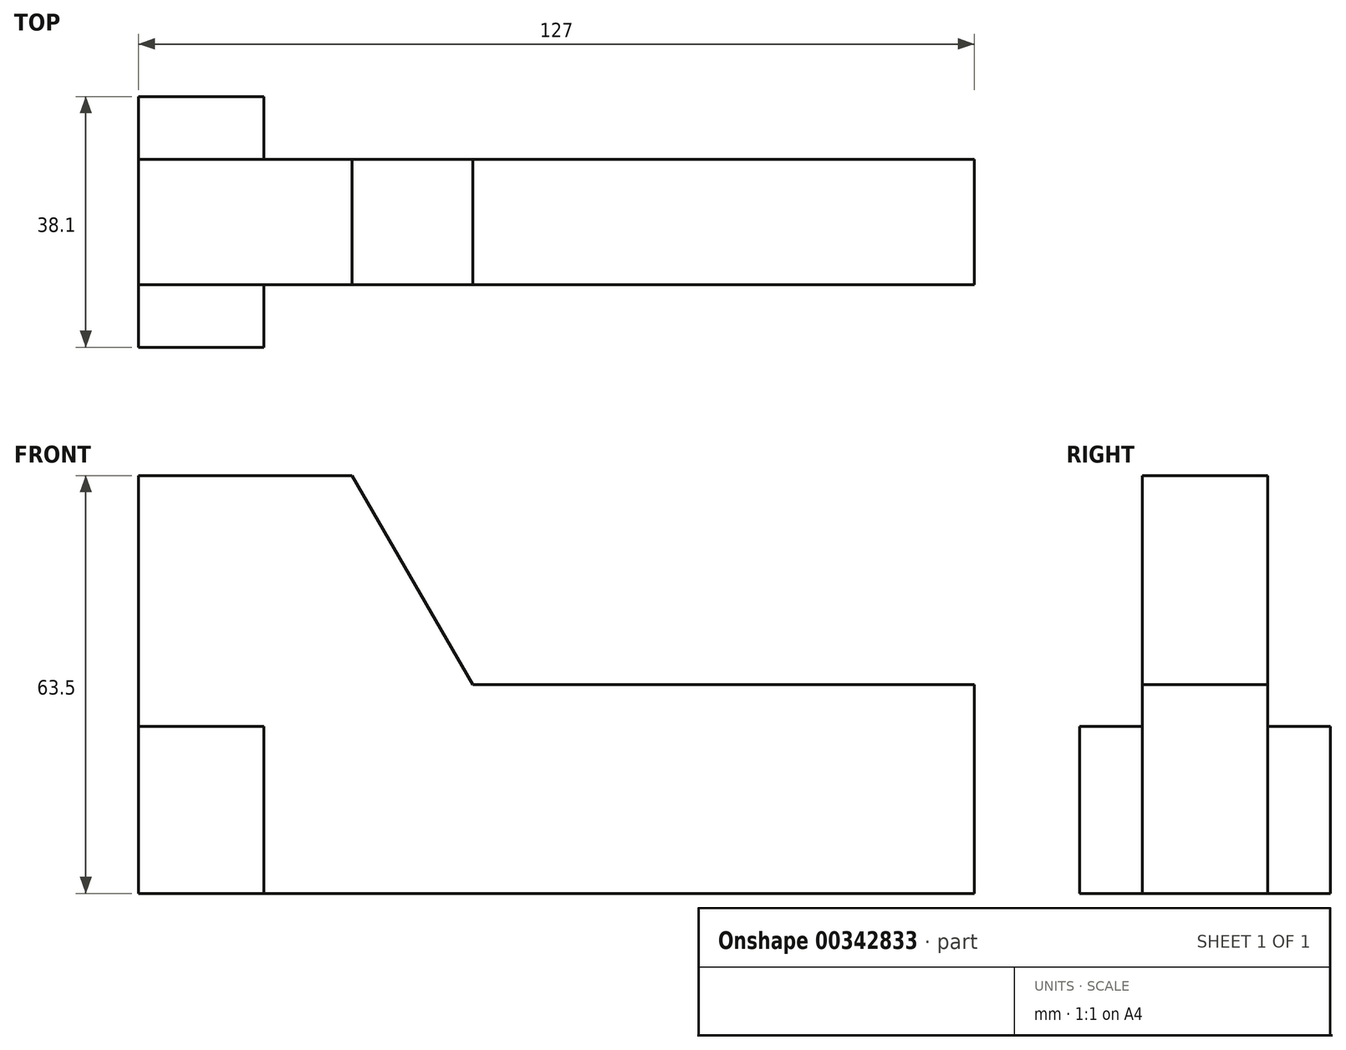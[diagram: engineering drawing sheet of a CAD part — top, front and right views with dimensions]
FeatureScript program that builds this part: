
annotation { "Feature Type Name" : "Feature", "Feature Type Description" : "" }
export const myFeature = defineFeature(function(context is Context, id is Id, definition is map)
    precondition{}
    {
        {
            var Q0;
            Q0=qCreatedBy(makeId("Front.planeOp"),FACE);
            var sketch = newSketch(context, id + "F0", { "sketchPlane" : qUnion([Q0])});
            skLineSegment(sketch, "E0", {"start": v(-49.55, -36.58) * mm, "end": v(77.45, -36.58) * mm});
            skLineSegment(sketch, "E1", {"start": v(77.45, -36.58) * mm, "end": v(77.45, -4.83) * mm});
            skLineSegment(sketch, "E2", {"start": v(77.45, -4.83) * mm, "end": v(1.25, -4.83) * mm});
            skLineSegment(sketch, "E3", {"start": v(-49.55, -36.58) * mm, "end": v(-49.55, 26.92) * mm});
            skLineSegment(sketch, "E4", {"start": v(-49.55, 26.92) * mm, "end": v(-17.08, 26.92) * mm});
            skLineSegment(sketch, "E5", {"start": v(1.25, -4.83) * mm, "end": v(-17.08, 26.92) * mm});
            skSolve(sketch);
        }
        {
            var Q0;
            Q0=makeQuery(id+"F0.imprint","IMPRINT",FACE,{"disambiguationData":[TD([[makeQuery(id+"F0.imprint","IMPRINT",EDGE,{"derivedFrom":sQuery(id+"F0.wireOp",EDGE,"E0")}),1.0]])]});
            extrude(context, id + "F1", {"entities" : qUnion([Q0]), "depth" : 19.05 * mm});
        }
        {
            var Q0;
            Q0=makeQuery(id+"F1.opExtrude","CAP_FACE",FACE,{"disambiguationData":[OSD([sQuery(id+"F0.wireOp",EDGE,"E0"),sQuery(id+"F0.wireOp",EDGE,"E1"),sQuery(id+"F0.wireOp",EDGE,"E2"),sQuery(id+"F0.wireOp",EDGE,"E3"),sQuery(id+"F0.wireOp",EDGE,"E4"),sQuery(id+"F0.wireOp",EDGE,"E5")])],"isStart":false});
            var sketch = newSketch(context, id + "F2", { "sketchPlane" : qUnion([Q0])});
            skLineSegment(sketch, "E6", {"start": v(-49.55, -36.58) * mm, "end": v(-49.55, -11.18) * mm});
            skLineSegment(sketch, "E7", {"start": v(-49.55, -11.18) * mm, "end": v(-30.5, -11.18) * mm});
            skLineSegment(sketch, "E8", {"start": v(-30.5, -11.18) * mm, "end": v(-30.5, -36.58) * mm});
            skLineSegment(sketch, "E9", {"start": v(-30.5, -36.58) * mm, "end": v(-49.55, -36.58) * mm});
            skSolve(sketch);
        }
        {
            var Q0;
            Q0=makeQuery(id+"F2.imprint","IMPRINT",FACE,{"disambiguationData":[TD([[makeQuery(id+"F2.imprint","IMPRINT",EDGE,{"derivedFrom":sQuery(id+"F2.wireOp",EDGE,"E6")}),-1.0]])]});
            extrude(context, id + "F3", {"entities" : qUnion([Q0]), "operationType" : NewBodyOperationType.ADD, "depth" : 9.52 * mm});
        }
        {
            var Q0;
            Q0=makeQuery(id+"F1.opExtrude","CAP_FACE",FACE,{"disambiguationData":[OSD([sQuery(id+"F0.wireOp",EDGE,"E0"),sQuery(id+"F0.wireOp",EDGE,"E1"),sQuery(id+"F0.wireOp",EDGE,"E2"),sQuery(id+"F0.wireOp",EDGE,"E3"),sQuery(id+"F0.wireOp",EDGE,"E4"),sQuery(id+"F0.wireOp",EDGE,"E5")])],"isStart":true});
            var sketch = newSketch(context, id + "F4", { "sketchPlane" : qUnion([Q0])});
            skLineSegment(sketch, "E10", {"start": v(49.55, -36.58) * mm, "end": v(30.5, -36.58) * mm});
            skLineSegment(sketch, "E11", {"start": v(30.5, -36.58) * mm, "end": v(30.5, -11.18) * mm});
            skLineSegment(sketch, "E12", {"start": v(30.5, -11.18) * mm, "end": v(49.55, -11.18) * mm});
            skLineSegment(sketch, "E13", {"start": v(49.55, -11.18) * mm, "end": v(49.55, -36.58) * mm});
            skSolve(sketch);
        }
        {
            var Q0;
            Q0=makeQuery(id+"F4.imprint","IMPRINT",FACE,{"disambiguationData":[TD([[makeQuery(id+"F4.imprint","IMPRINT",EDGE,{"derivedFrom":sQuery(id+"F4.wireOp",EDGE,"E10")}),-1.0]])]});
            extrude(context, id + "F5", {"entities" : qUnion([Q0]), "operationType" : NewBodyOperationType.ADD, "depth" : 9.52 * mm});
        }
    });
